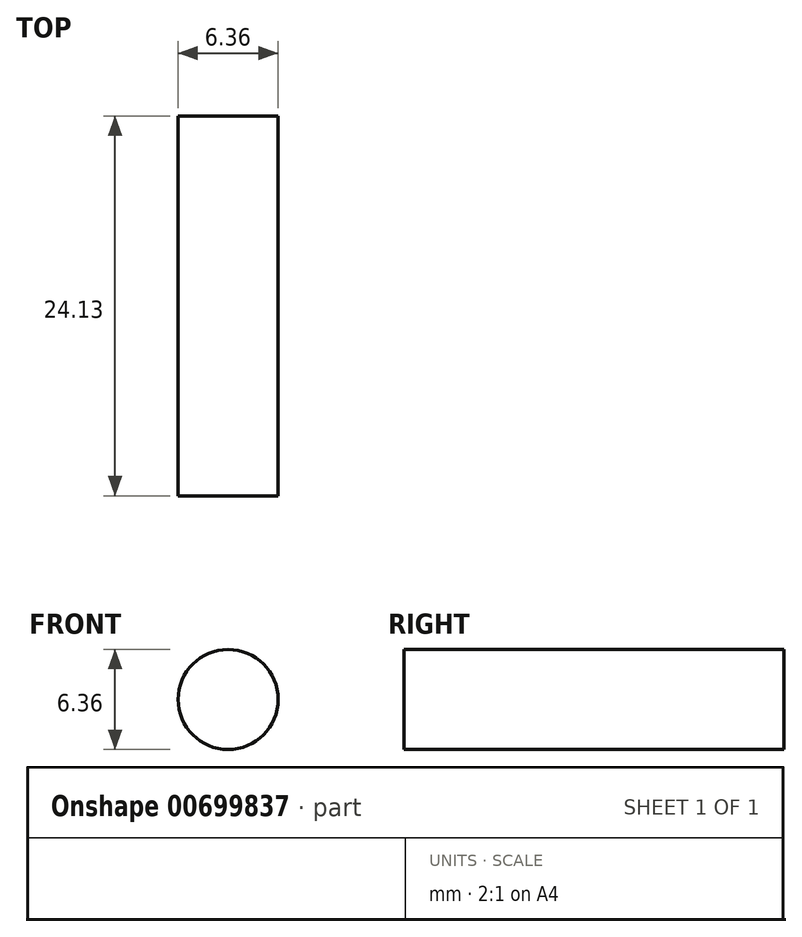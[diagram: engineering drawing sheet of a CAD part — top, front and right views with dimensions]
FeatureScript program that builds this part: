
annotation { "Feature Type Name" : "Feature", "Feature Type Description" : "" }
export const myFeature = defineFeature(function(context is Context, id is Id, definition is map)
    precondition{}
    {
        {
            var Q0;
            Q0=qCreatedBy(makeId("Front.planeOp"),FACE);
            var sketch = newSketch(context, id + "F0", { "sketchPlane" : qUnion([Q0])});
            skCircle(sketch, "E0", {"center": v(0, 0) * mm, "radius": 3.17 * mm});
            skSolve(sketch);
        }
        {
            var Q0;
            Q0=qSketchRegion(id+"F0",true);
            extrude(context, id + "F1", {"entities" : qUnion([Q0]), "depth" : 24.13 * mm});
        }
    });
